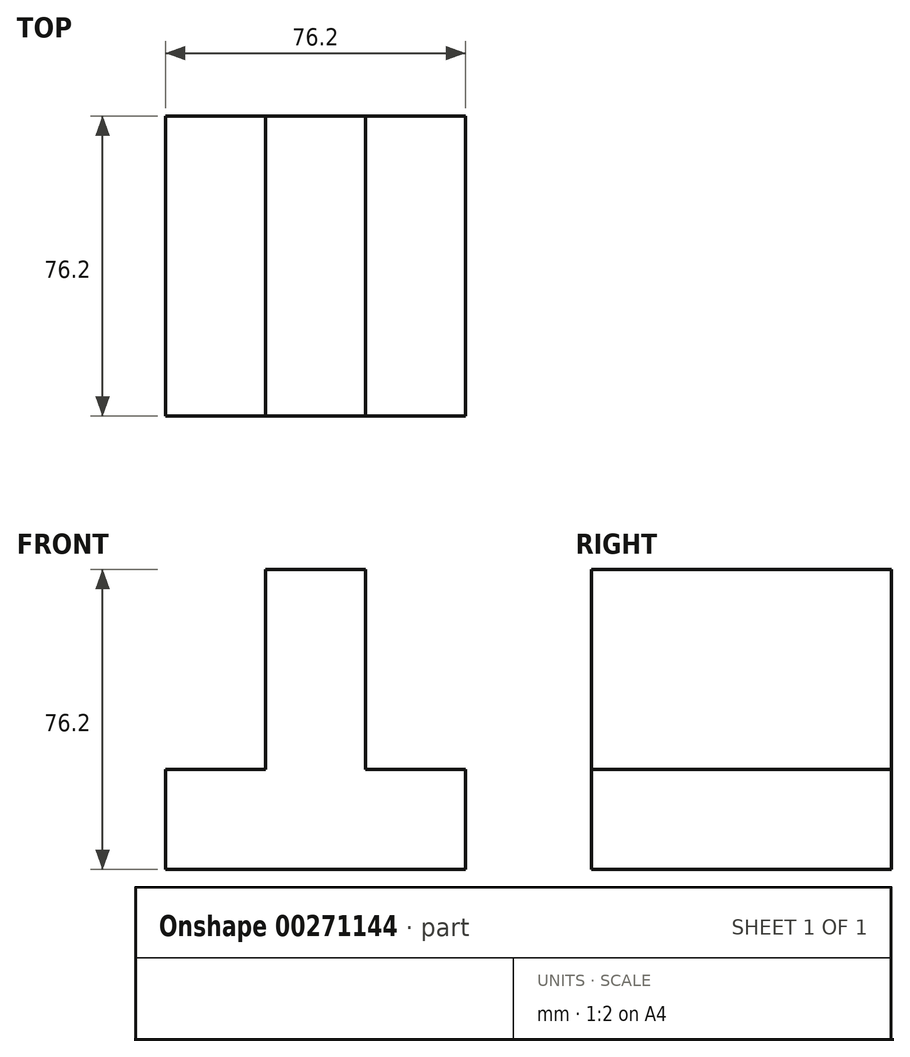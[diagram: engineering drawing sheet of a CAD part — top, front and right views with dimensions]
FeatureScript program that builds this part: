
annotation { "Feature Type Name" : "Feature", "Feature Type Description" : "" }
export const myFeature = defineFeature(function(context is Context, id is Id, definition is map)
    precondition{}
    {
        {
            var Q0;
            Q0=qCreatedBy(makeId("Front.planeOp"),FACE);
            var sketch = newSketch(context, id + "F0", { "sketchPlane" : qUnion([Q0])});
            skLineSegment(sketch, "E0", {"start": v(-52.13, -59) * mm, "end": v(24.07, -59) * mm});
            skLineSegment(sketch, "E1", {"start": v(24.07, -59) * mm, "end": v(24.07, -33.6) * mm});
            skLineSegment(sketch, "E2", {"start": v(24.07, -33.6) * mm, "end": v(-1.33, -33.6) * mm});
            skLineSegment(sketch, "E3", {"start": v(-1.33, -33.6) * mm, "end": v(-1.33, 17.2) * mm});
            skLineSegment(sketch, "E4", {"start": v(-1.33, 17.2) * mm, "end": v(-26.73, 17.2) * mm});
            skLineSegment(sketch, "E5", {"start": v(-26.73, 17.2) * mm, "end": v(-26.73, -33.6) * mm});
            skLineSegment(sketch, "E6", {"start": v(-26.73, -33.6) * mm, "end": v(-52.13, -33.6) * mm});
            skLineSegment(sketch, "E7", {"start": v(-52.13, -33.6) * mm, "end": v(-52.13, -59) * mm});
            skSolve(sketch);
        }
        {
            var Q0;
            Q0 = qSketchRegion(id + "F0", true);
            extrude(context, id + "F1", {"entities" : qUnion([Q0]), "depth" : 76.2 * mm});
        }
    });
